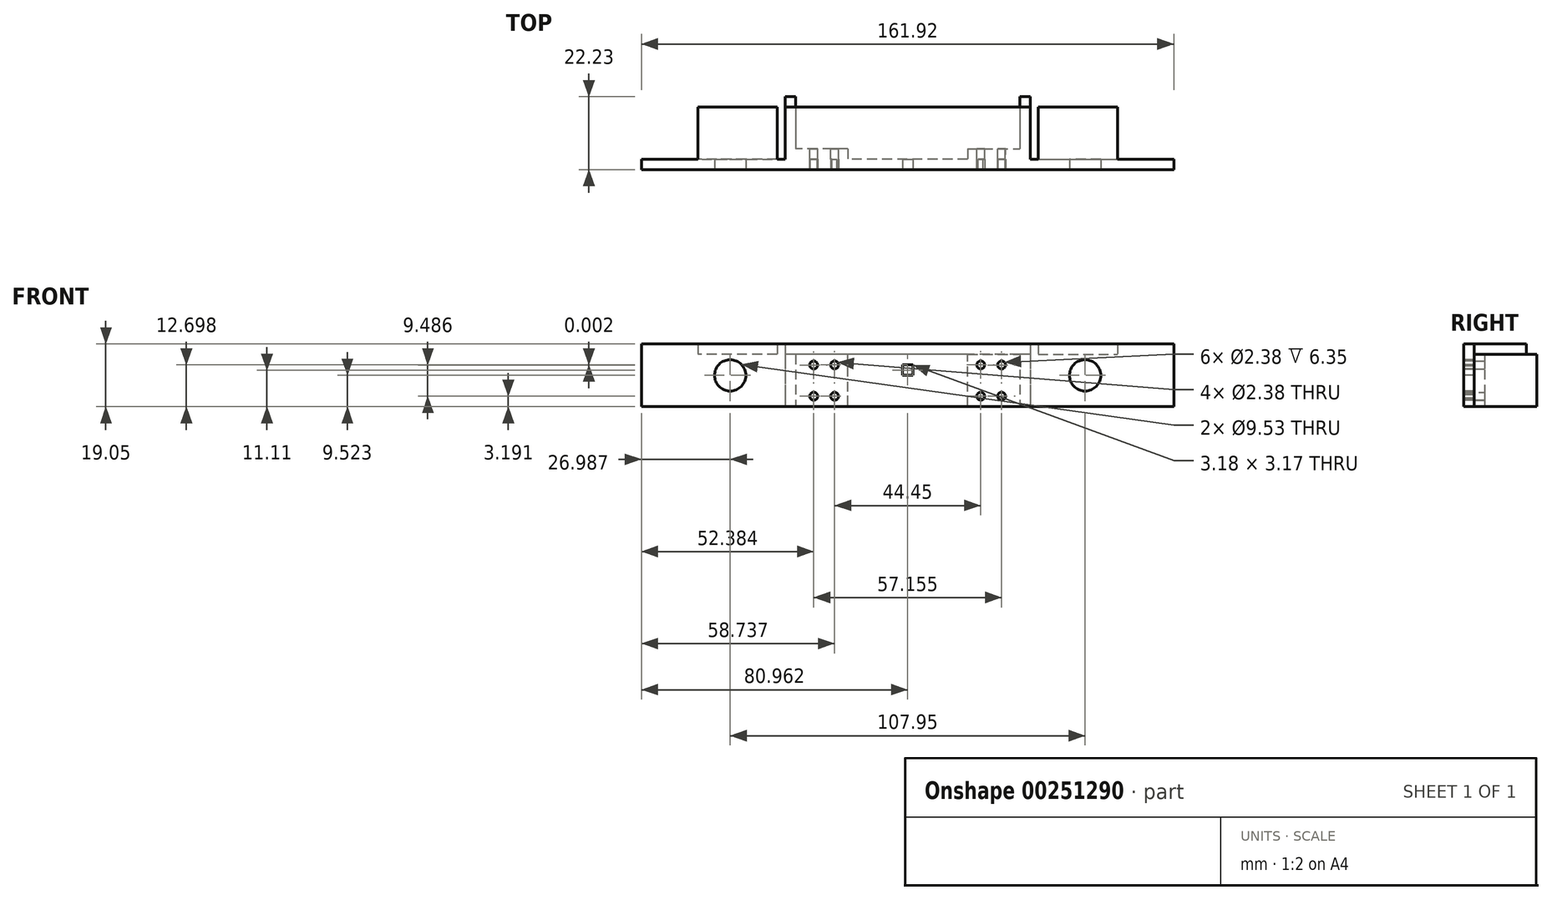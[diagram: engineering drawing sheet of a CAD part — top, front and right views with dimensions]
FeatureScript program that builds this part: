
annotation { "Feature Type Name" : "Feature", "Feature Type Description" : "" }
export const myFeature = defineFeature(function(context is Context, id is Id, definition is map)
    precondition{}
    {
        {
            var Q0;
            Q0=qCreatedBy(makeId("Front.planeOp"),FACE);
            var sketch = newSketch(context, id + "F0", { "sketchPlane" : qUnion([Q0])});
            skLineSegment(sketch, "E0", {"start": v(-49.52, -7.96) * mm, "end": v(112.4, -7.96) * mm});
            skLineSegment(sketch, "E1", {"start": v(112.4, -7.96) * mm, "end": v(112.4, 11.09) * mm});
            skLineSegment(sketch, "E2", {"start": v(112.4, 11.09) * mm, "end": v(-49.52, 11.09) * mm});
            skLineSegment(sketch, "E3", {"start": v(-49.52, 11.09) * mm, "end": v(-49.52, -7.96) * mm});
            skSolve(sketch);
        }
        {
            var Q0;
            Q0 = qSketchRegion(id + "F0", true);
            extrude(context, id + "F1", {"entities" : qUnion([Q0]), "depth" : 3.17 * mm});
        }
        {
            var Q0;
            Q0=makeQuery(id+"F1.opExtrude","CAP_FACE",FACE,{"disambiguationData":[OSD([sQuery(id+"F0.wireOp",EDGE,"E0"),sQuery(id+"F0.wireOp",EDGE,"E1"),sQuery(id+"F0.wireOp",EDGE,"E2"),sQuery(id+"F0.wireOp",EDGE,"E3")])],"isStart":false});
            var sketch = newSketch(context, id + "F2", { "sketchPlane" : qUnion([Q0])});
            skCircle(sketch, "E4", {"center": v(-22.53, 1.56) * mm, "radius": 4.76 * mm});
            skCircle(sketch, "E5", {"center": v(2.87, 4.74) * mm, "radius": 1.2 * mm});
            skCircle(sketch, "E6", {"center": v(2.87, -4.79) * mm, "radius": 1.2 * mm});
            skLineSegment(sketch, "E7", {"start": v(31.44, 11.09) * mm, "end": v(31.44, -7.96) * mm});
            skPoint(sketch, "E8.oppositeSnap0", {"position": v(31.44, 1.56) * mm});
            skLineSegment(sketch, "E8.bottom", {"start": v(29.85, 4.74) * mm, "end": v(33.03, 4.74) * mm});
            skLineSegment(sketch, "E8.top", {"start": v(29.85, 1.56) * mm, "end": v(33.03, 1.56) * mm});
            skLineSegment(sketch, "E8.left", {"start": v(29.85, 4.74) * mm, "end": v(29.85, 1.56) * mm});
            skLineSegment(sketch, "E8.right", {"start": v(33.03, 4.74) * mm, "end": v(33.03, 1.56) * mm});
            skCircle(sketch, "E9.MirrorC", {"center": v(85.42, 1.56) * mm, "radius": 4.76 * mm});
            skCircle(sketch, "E10", {"center": v(9.22, 4.74) * mm, "radius": 1.2 * mm});
            skCircle(sketch, "E11", {"center": v(9.22, -4.79) * mm, "radius": 1.2 * mm});
            skCircle(sketch, "E12.MirrorC", {"center": v(53.67, -4.79) * mm, "radius": 1.2 * mm});
            skCircle(sketch, "E13.MirrorC", {"center": v(53.67, 4.74) * mm, "radius": 1.2 * mm});
            skCircle(sketch, "E14.MirrorC", {"center": v(60.02, 4.74) * mm, "radius": 1.2 * mm});
            skCircle(sketch, "E15.MirrorC", {"center": v(60.02, -4.79) * mm, "radius": 1.2 * mm});
            skSolve(sketch);
        }
        {
            var Q0;
            Q0 = qSketchRegion(id + "F2", true);
            extrude(context, id + "F3", {"entities" : qUnion([Q0]), "operationType" : NewBodyOperationType.REMOVE, "oppositeDirection" : true, "depth" : 6.35 * mm});
        }
        {
            var Q0;
            Q0=makeQuery(id+"F1.opExtrude","CAP_FACE",FACE,{"disambiguationData":[OSD([sQuery(id+"F0.wireOp",EDGE,"E0"),sQuery(id+"F0.wireOp",EDGE,"E1"),sQuery(id+"F0.wireOp",EDGE,"E2"),sQuery(id+"F0.wireOp",EDGE,"E3")])],"isStart":true});
            var sketch = newSketch(context, id + "F4", { "sketchPlane" : qUnion([Q0])});
            skLineSegment(sketch, "E16", {"start": v(-95.26, 11.09) * mm, "end": v(-95.26, 7.91) * mm});
            skLineSegment(sketch, "E17", {"start": v(32.38, 11.09) * mm, "end": v(32.38, 7.91) * mm});
            skLineSegment(sketch, "E18", {"start": v(5.86, 11.09) * mm, "end": v(5.86, 7.91) * mm});
            skLineSegment(sketch, "E19", {"start": v(-68.75, 11.09) * mm, "end": v(-68.75, 7.91) * mm});
            skLineSegment(sketch, "E20", {"start": v(-68.75, 7.91) * mm, "end": v(5.86, 7.91) * mm});
            skLineSegment(sketch, "E21", {"start": v(-71.13, 11.09) * mm, "end": v(-71.13, 7.91) * mm});
            skLineSegment(sketch, "E22", {"start": v(-71.13, 7.91) * mm, "end": v(-95.26, 7.91) * mm});
            skLineSegment(sketch, "E23", {"start": v(8.25, 11.09) * mm, "end": v(8.25, 7.91) * mm});
            skLineSegment(sketch, "E24", {"start": v(8.25, 7.91) * mm, "end": v(32.38, 7.91) * mm});
            skLineSegment(sketch, "E25", {"start": v(-49.7, 7.91) * mm, "end": v(-49.7, -7.96) * mm});
            skLineSegment(sketch, "E26", {"start": v(-13.19, 7.91) * mm, "end": v(-13.19, -7.96) * mm});
            skLineSegment(sketch, "E27", {"start": v(-68.75, 7.91) * mm, "end": v(-68.75, -7.96) * mm});
            skLineSegment(sketch, "E28", {"start": v(-68.75, -7.96) * mm, "end": v(-65.57, -7.96) * mm});
            skLineSegment(sketch, "E29", {"start": v(-65.57, -7.96) * mm, "end": v(-65.57, 7.91) * mm});
            skLineSegment(sketch, "E30", {"start": v(5.86, 7.91) * mm, "end": v(5.86, -7.96) * mm});
            skLineSegment(sketch, "E31", {"start": v(5.86, -7.96) * mm, "end": v(2.69, -7.96) * mm});
            skLineSegment(sketch, "E32", {"start": v(2.69, -7.96) * mm, "end": v(2.69, 7.91) * mm});
            skSolve(sketch);
        }
        {
            var Q0;
            Q0 = qSketchRegion(id + "F2", true);
            extrude(context, id + "F5", {"entities" : qUnion([Q0]), "operationType" : NewBodyOperationType.REMOVE, "oppositeDirection" : true, "depth" : 25.4 * mm});
        }
        {
            var Q0;
            {var subQ0=sQuery(id+"F4.wireOp",EDGE,"E27");Q0=makeQuery(id+"F4.imprint","IMPRINT",FACE,{"disambiguationData":[TD([[makeQuery(id+"F4.imprint","IMPRINT",EDGE,{"derivedFrom":subQ0}),1.0]])]});}
            var Q1;
            {var subQ0=sQuery(id+"F4.wireOp",EDGE,"E30");Q1=makeQuery(id+"F4.imprint","IMPRINT",FACE,{"disambiguationData":[TD([[makeQuery(id+"F4.imprint","IMPRINT",EDGE,{"derivedFrom":subQ0}),-1.0]])]});}
            extrude(context, id + "F6", {"entities" : qUnion([Q0, Q1]), "operationType" : NewBodyOperationType.ADD, "depth" : 19.05 * mm});
        }
        {
            var Q0;
            Q0=makeQuery(id+"F6.opExtrude","SWEPT_FACE",FACE,{"disambiguationData":[OSD([sQuery(id+"F4.wireOp",EDGE,"E29")])]});
            var sketch = newSketch(context, id + "F7", { "sketchPlane" : qUnion([Q0])});
            skLineSegment(sketch, "E33", {"start": v(-3.18, 7.91) * mm, "end": v(-3.17, -7.96) * mm});
            skSolve(sketch);
        }
        {
            var Q0;
            Q0 = qSketchRegion(id + "F7", true);
            var Q1;
            {var subQ0=sQuery(id+"F7.wireOp",EDGE,"E33");Q1=makeQuery(id+"F7.imprint","IMPRINT",FACE,{"disambiguationData":[TD([[makeQuery(id+"F7.imprint","IMPRINT",EDGE,{"derivedFrom":subQ0}),1.0]])]});}
            extrude(context, id + "F8", {"entities" : qUnion([Q0, Q1]), "operationType" : NewBodyOperationType.ADD, "depth" : 15.88 * mm});
        }
        {
            var Q0;
            Q0=makeQuery(id+"F6.opExtrude","SWEPT_FACE",FACE,{"disambiguationData":[OSD([sQuery(id+"F4.wireOp",EDGE,"E32")])]});
            var sketch = newSketch(context, id + "F9", { "sketchPlane" : qUnion([Q0])});
            skLineSegment(sketch, "E34", {"start": v(3.17, 7.91) * mm, "end": v(3.18, -7.96) * mm});
            skSolve(sketch);
        }
        {
            var Q0;
            Q0 = qSketchRegion(id + "F9", true);
            var Q1;
            {var subQ0=sQuery(id+"F9.wireOp",EDGE,"E34");Q1=makeQuery(id+"F9.imprint","IMPRINT",FACE,{"disambiguationData":[TD([[makeQuery(id+"F9.imprint","IMPRINT",EDGE,{"derivedFrom":subQ0}),-1.0]])]});}
            extrude(context, id + "F10", {"entities" : qUnion([Q0, Q1]), "operationType" : NewBodyOperationType.ADD, "depth" : 15.88 * mm});
        }
        {
            var Q0;
            Q0 = qSketchRegion(id + "F4", true);
            var Q1;
            {var subQ0=sQuery(id+"F4.wireOp",EDGE,"E16");Q1=makeQuery(id+"F4.imprint","IMPRINT",FACE,{"disambiguationData":[TD([[makeQuery(id+"F4.imprint","IMPRINT",EDGE,{"derivedFrom":subQ0}),1.0]])]});}
            var Q2;
            {var subQ5=sQuery(id+"F4.wireOp",EDGE,"E18");Q2=makeQuery(id+"F4.imprint","IMPRINT",FACE,{"disambiguationData":[TD([[makeQuery(id+"F4.imprint","IMPRINT",EDGE,{"derivedFrom":subQ5}),-1.0]])]});}
            var Q3;
            {var subQ0=sQuery(id+"F4.wireOp",EDGE,"E17");Q3=makeQuery(id+"F4.imprint","IMPRINT",FACE,{"disambiguationData":[TD([[makeQuery(id+"F4.imprint","IMPRINT",EDGE,{"derivedFrom":subQ0}),-1.0]])]});}
            extrude(context, id + "F11", {"entities" : qUnion([Q0, Q1, Q2, Q3]), "operationType" : NewBodyOperationType.ADD, "depth" : 15.88 * mm});
        }
        {
            var Q0;
            Q0=makeQuery(id+"F10.opExtrude","SWEPT_FACE",FACE,{"disambiguationData":[OSD([sQuery(id+"F9.wireOp",EDGE,"E34")])]});
            var sketch = newSketch(context, id + "F12", { "sketchPlane" : qUnion([Q0])});
            skCircle(sketch, "E35", {"center": v(-9.22, 4.74) * mm, "radius": 1.2 * mm});
            skCircle(sketch, "E36", {"center": v(-9.24, -4.77) * mm, "radius": 1.2 * mm});
            skCircle(sketch, "E37", {"center": v(-2.89, -4.74) * mm, "radius": 1.2 * mm});
            skCircle(sketch, "E38", {"center": v(-2.86, 4.72) * mm, "radius": 1.2 * mm});
            skCircle(sketch, "E39.MirrorC", {"center": v(-53.66, 4.74) * mm, "radius": 1.2 * mm});
            skCircle(sketch, "E40.MirrorC", {"center": v(-60.02, 4.72) * mm, "radius": 1.2 * mm});
            skCircle(sketch, "E41.MirrorC", {"center": v(-53.64, -4.77) * mm, "radius": 1.2 * mm});
            skCircle(sketch, "E42.MirrorC", {"center": v(-60, -4.74) * mm, "radius": 1.2 * mm});
            skSolve(sketch);
        }
        {
            var Q0;
            Q0 = qSketchRegion(id + "F12", true);
            extrude(context, id + "F13", {"entities" : qUnion([Q0]), "operationType" : NewBodyOperationType.REMOVE, "oppositeDirection" : true, "depth" : 25.4 * mm});
        }
    });
